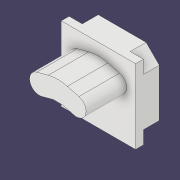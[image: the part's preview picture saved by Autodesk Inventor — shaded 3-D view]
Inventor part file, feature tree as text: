
AUTODESK INVENTOR PART (.ipt)
format: ipt  version: 2017 SP1 (Build 210196100, 196)  size: 143,360 bytes
history: native  units: in
note: dims shown in document units (in); Inventor stores cm internally (conversion verified against a paired STEP export)
features: extrude x3, sketch x3
ambient origin geometry x8: Origin, YZ Plane, XZ Plane, XY Plane, X Axis, Y Axis, Z Axis, Center Point
bodies: Solid1 (feature_tree)
feature tree (6):
  extrude  "Extrusion1"  Depth=24.4094in
  extrude  "Extrusion2"  Depth=7.7953in TaperAngle=0.0deg
  extrude  "Extrusion3"  Depth=13.3465in
  sketch  "Sketch1"  dims[d0=24.4094in d1=24.4094in]
  sketch  "Sketch2"  dims[d2=7.3031in d3=7.7953in d4=0.0in]
  sketch  "Sketch3"  dims[d5=4.3307in d6=4.3307in d7=1.5748in d9=360.0deg d11=5.2362in d12=0.0in d32=6.2992in d33=3.937in d34=3.937in d35=6.2992in d36=6.2992in d37=6.2992in d38=75.0deg d39=75.0deg d40=6.2992in d41=3.937in d42=3.937in d43=0.4134in d44=0.4134in d45=4.4488in d46=8.3858in d47=0.7874in d48=12.4016in d49=0.4134in d50=0.597in d51=7.3031in d52=13.3465in d53=0.0in]
